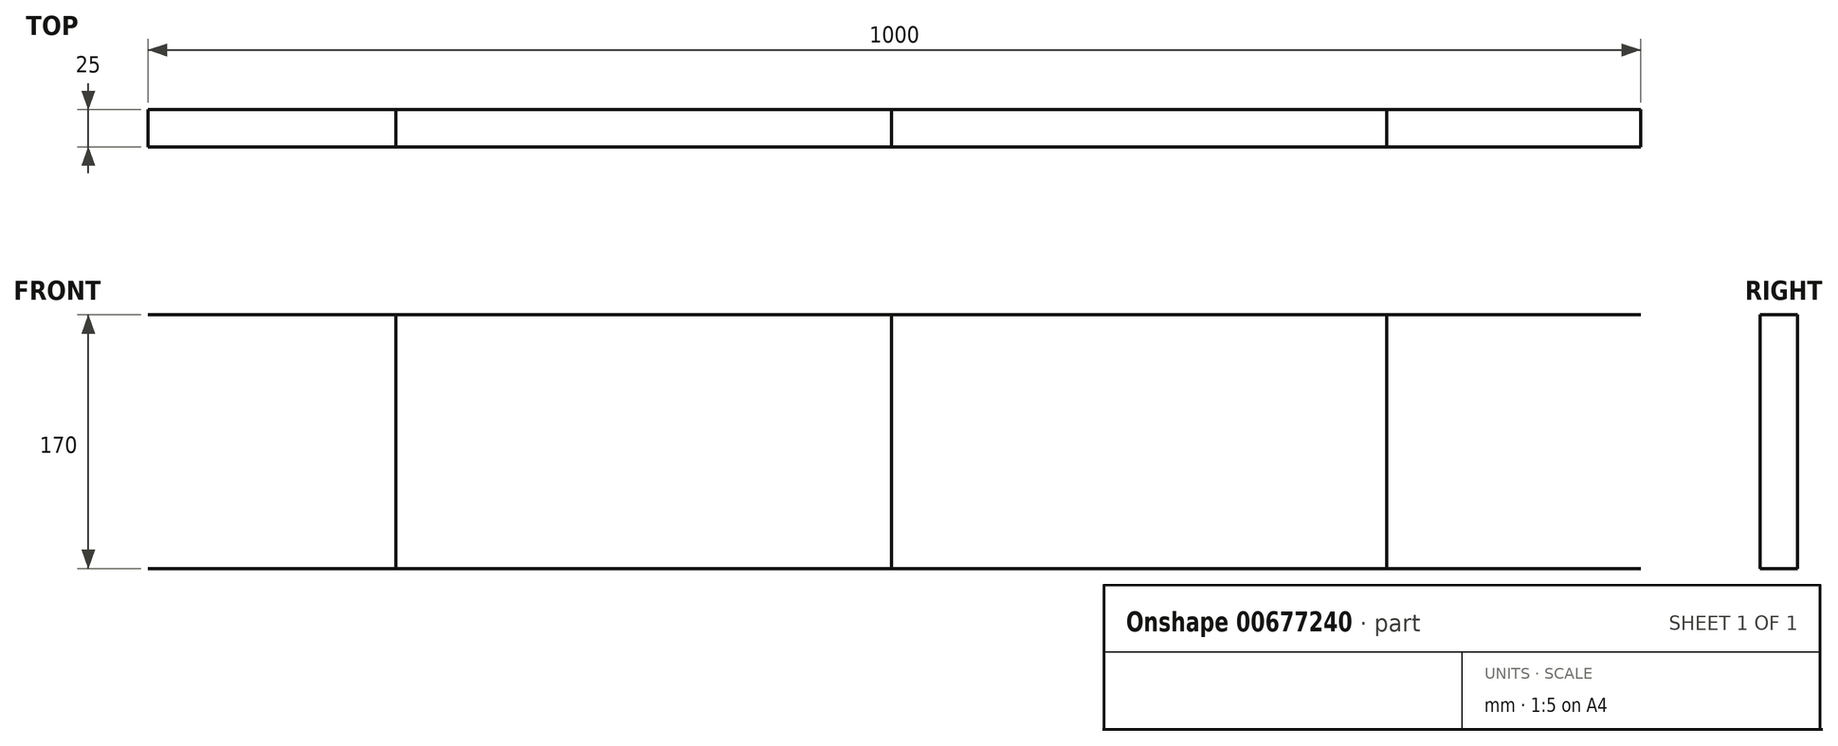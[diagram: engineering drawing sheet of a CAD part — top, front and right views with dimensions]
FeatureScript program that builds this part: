
annotation { "Feature Type Name" : "Feature", "Feature Type Description" : "" }
export const myFeature = defineFeature(function(context is Context, id is Id, definition is map)
    precondition{}
    {
        {
            var Q0;
            Q0=qCreatedBy(makeId("Front.planeOp"),FACE);
            var sketch = newSketch(context, id + "F0", { "sketchPlane" : qUnion([Q0])});
            skLineSegment(sketch, "E0.bottom", {"start": v(-486.97, 230.87) * mm, "end": v(513.03, 230.87) * mm});
            skLineSegment(sketch, "E0.top", {"start": v(-486.97, -99.13) * mm, "end": v(513.03, -99.13) * mm});
            skLineSegment(sketch, "E0.left", {"start": v(-486.97, 230.87) * mm, "end": v(-486.97, -99.13) * mm});
            skLineSegment(sketch, "E0.right", {"start": v(513.03, 230.87) * mm, "end": v(513.03, -99.13) * mm});
            skLineSegment(sketch, "E1", {"start": v(-486.97, 155.87) * mm, "end": v(513.03, 155.87) * mm});
            skLineSegment(sketch, "E2", {"start": v(-486.97, -14.13) * mm, "end": v(513.03, -14.13) * mm});
            skLineSegment(sketch, "E3", {"start": v(-320.97, 155.87) * mm, "end": v(-320.97, -14.13) * mm});
            skLineSegment(sketch, "E4", {"start": v(11.03, 155.87) * mm, "end": v(11.03, -14.13) * mm});
            skLineSegment(sketch, "E5", {"start": v(343.03, 155.87) * mm, "end": v(343.03, -14.13) * mm});
            skSolve(sketch);
        }
        {
            var Q0;
            Q0=sQuery(id+"F0.wireOp",EDGE,"E3");
            var Q1;
            Q1=sQuery(id+"F0.wireOp",EDGE,"E4");
            var Q2;
            Q2=sQuery(id+"F0.wireOp",EDGE,"E5");
            extrude(context, id + "F1", {"bodyType" : ToolBodyType.SURFACE, "surfaceEntities" : qUnion([Q0, Q1, Q2]), "depth" : 25 * mm, "offsetDistance" : 25 * mm});
        }
        {
            var Q0;
            Q0=sQuery(id+"F0.wireOp",EDGE,"E1");
            var Q1;
            Q1=sQuery(id+"F0.wireOp",EDGE,"E2");
            extrude(context, id + "F2", {"bodyType" : ToolBodyType.SURFACE, "surfaceEntities" : qUnion([Q0, Q1]), "depth" : 25 * mm, "offsetDistance" : 25 * mm});
        }
    });
